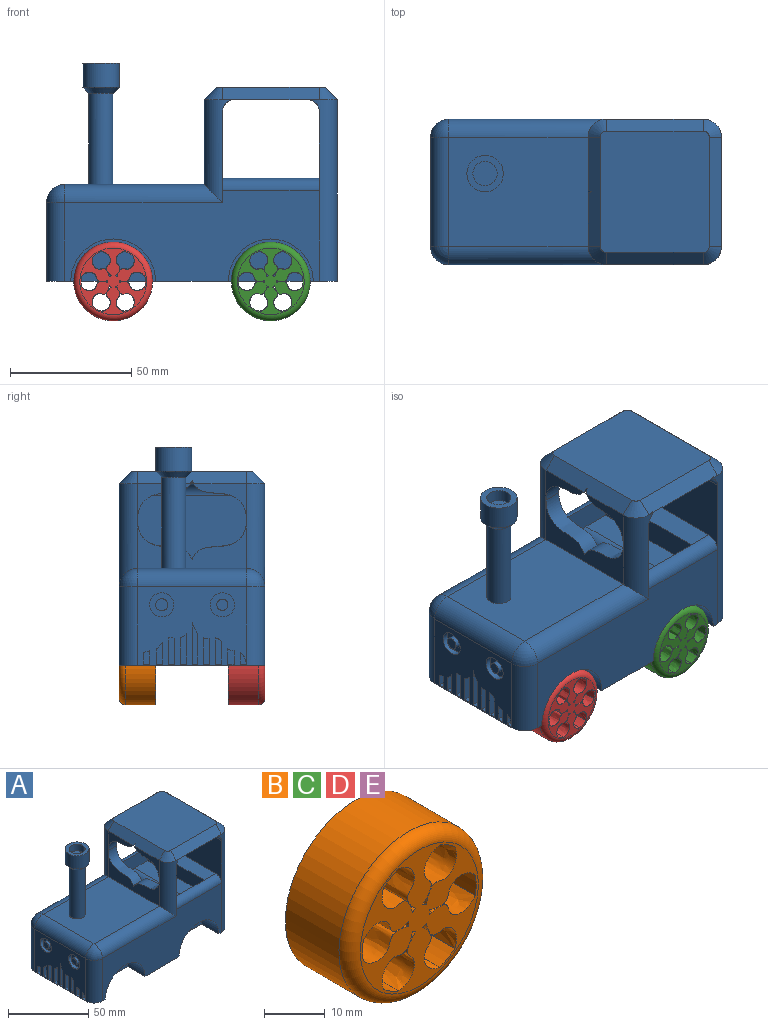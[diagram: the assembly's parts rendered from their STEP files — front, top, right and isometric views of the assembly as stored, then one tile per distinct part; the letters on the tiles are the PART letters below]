
ASSEMBLY  parts=5 mates=4
PART A: 116 faces, bbox 120.1x60.1x90.1 mm
  f0: plane 45x32.5mm, normal (-1,0,0), area 1108mm2, adj f4,f20,f22,f23,f52,f55,f56,f57
  f1: plane 22.46x15.71mm, normal (-1,0,0), area 101.4mm2, adj f18,f32,f38
  f2: plane 22.54x15.71mm, normal (-1,0,0), area 100.8mm2, adj f25,f29,f38
  f3: plane 105x37.5mm, normal (0,1,0), area 2650.4mm2, adj f4,f14,f16,f23,f25,f26,f28,f46
  f4: plane 120x60mm, normal (0,0,-1), area 5051.7mm2, adj f0,f3,f6,f7,f10,f11,f12,f13
  f5: plane 50x45mm, normal (0,0,1), area 2244.6mm2, adj f34,f35,f36,f37,f38,f39,f40,f41
  f6: plane 105x37.5mm, normal (0,-1,0), area 2650.4mm2, adj f4,f10,f12,f18,f19,f20,f27,f50
  f7: plane 75x45mm, normal (1,0,0), area 3375mm2, adj f4,f27,f28,f37
  f8: plane 57.5x45mm, normal (0,0,1), area 2509mm2, adj f9,f19,f22,f26,f103
  f9: plane 45x20mm, normal (-1,0,0), area 426.2mm2, adj f8,f18,f25,f30,f31
  f10: cylinder r=17.5mm len=35mm, axis (0,-1,0), area 824.7mm2, adj f4,f6,f11
  f11: plane 35x17.5mm, normal (0,-1,0), area 481.1mm2, adj f4,f10
  f12: cylinder r=17.5mm len=35mm, axis (0,-1,0), area 824.7mm2, adj f4,f6,f13
  f13: plane 35x17.5mm, normal (0,-1,0), area 481.1mm2, adj f4,f12
  f14: cylinder r=17.5mm len=35mm, axis (0,1,0), area 824.7mm2, adj f3,f4,f15
  f15: plane 35x17.5mm, normal (0,1,0), area 481.1mm2, adj f4,f14
  f16: cylinder r=17.5mm len=35mm, axis (0,1,0), area 824.7mm2, adj f3,f4,f17
  f17: plane 35x17.5mm, normal (0,1,0), area 481.1mm2, adj f4,f16
  f18: cylinder r=7.5mm len=42.5mm, axis (0,0,-1), area 449.9mm2, adj f1,f6,f9,f19,f40,f43,f45,f47
  f19: cylinder r=7.5mm len=65mm, axis (-1,0,0), area 709.5mm2, adj f6,f8,f18,f21
  f20: cylinder r=7.5mm len=32.5mm, axis (0,0,-1), area 382.9mm2, adj f0,f4,f6,f21
  f21: sphere r=7.5mm, area 88.4mm2, adj f19,f20,f22
  f22: cylinder r=7.5mm len=45mm, axis (0,1,0), area 530.1mm2, adj f0,f8,f21,f24
  f23: cylinder r=7.5mm len=32.5mm, axis (0,0,1), area 382.9mm2, adj f0,f3,f4,f24
  f24: sphere r=7.5mm, area 88.4mm2, adj f22,f23,f26
  f25: cylinder r=7.5mm len=42.5mm, axis (0,0,1), area 449.9mm2, adj f2,f3,f9,f26,f36,f43,f45,f49
  f26: cylinder r=7.5mm len=65mm, axis (1,0,0), area 709.5mm2, adj f3,f8,f24,f25
  f27: cylinder r=7.5mm len=75mm, axis (0,0,1), area 889.1mm2, adj f4,f6,f7,f39,f44,f45,f48
  f28: cylinder r=7.5mm len=75mm, axis (0,0,-1), area 889.1mm2, adj f3,f4,f7,f35,f44,f45,f48
  f29: extruded ~25x22.54mm, area 266.2mm2, adj f2,f30,f32,f33,f38,f43,f45,f49
  f30: extruded ~22.54x16.26mm, area 233.4mm2, adj f9,f29,f31,f43
  f31: extruded ~22.46x16.26mm, area 232.6mm2, adj f9,f30,f32,f43
  f32: extruded ~25x22.46mm, area 265.3mm2, adj f1,f29,f31,f33,f38,f43,f45,f47
  f33: plane 1.36x1.27mm, normal (-1,0,0), area 0.8mm2, adj f29,f32,f45
  f34: plane 40x5mm, normal (0,0.71,0.71), area 282.8mm2, adj f5,f35,f36,f45
  f35: cone r=2.5mm half-angle=45deg, axis (0,0,-1), area 55.5mm2, adj f5,f28,f34,f37
  f36: cone r=2.5mm half-angle=45deg, axis (0,0,-1), area 55.5mm2, adj f5,f25,f34,f38
  f37: plane 45x5mm, normal (0.71,0,0.71), area 318.2mm2, adj f5,f7,f35,f39
  f38: plane 45.05x5.05mm, normal (-0.71,0,0.71), area 317.1mm2, adj f1,f2,f5,f29,f32,f36,f40
  f39: cone r=2.5mm half-angle=45deg, axis (0,0,-1), area 55.5mm2, adj f5,f27,f37,f41
  f40: cone r=2.5mm half-angle=45deg, axis (0,0,-1), area 55.5mm2, adj f5,f18,f38,f41
  f41: plane 40x5mm, normal (0,-0.71,0.71), area 282.8mm2, adj f5,f39,f40,f45
  f42: plane 50x10.25mm, normal (0,0,1), area 512.5mm2, adj f44,f46,f50,f113
  f43: plane 60x52.85mm, normal (1,0,0), area 2018.2mm2, adj f18,f25,f29,f30,f31,f32,f46,f47
  f44: plane 60x32.5mm, normal (-1,0,0), area 1660.7mm2, adj f27,f28,f42,f46,f48,f50
  f45: plane 60x40mm, normal (0,0,-1), area 1795.2mm2, adj f18,f25,f27,f28,f29,f32,f33,f34
  f46: cylinder r=5mm len=40mm, axis (1,0,0), area 314.2mm2, adj f3,f42,f43,f44,f110
  f47: cylinder r=5mm len=29.29mm, axis (0,1,0), area 201.9mm2, adj f18,f32,f43,f45
  f48: cylinder r=5mm len=60mm, axis (0,1,0), area 464.8mm2, adj f27,f28,f44,f45
  f49: cylinder r=5mm len=29.36mm, axis (0,1,0), area 201.7mm2, adj f25,f29,f43,f45
  f50: cylinder r=5mm len=40mm, axis (-1,0,0), area 314.2mm2, adj f6,f42,f43,f44,f111
  f51: cylinder r=2.5mm len=5mm, axis (-1,0,0), area 39.3mm2, adj f53,f54
  f52: cylinder r=5mm len=10mm, axis (-1,0,0), area 78.5mm2, adj f0,f53
  f53: plane 10x10mm, normal (-1,0,0), area 58.9mm2, adj f51,f52
  f54: plane 5x5mm, normal (-1,0,0), area 19.6mm2, adj f51
  f55: extruded ~4.84x2.5mm, area 14.2mm2, adj f0,f56,f57,f58
  f56: plane 4.84x2.5mm, normal (0,-1,0), area 12.1mm2, adj f0,f55,f57,f58
  f57: plane 2.5x2.5mm, normal (0,0,1), area 6.2mm2, adj f0,f55,f56,f58
  f58: plane 4.84x2.5mm, normal (-1,0,0), area 8.6mm2, adj f55,f56,f57
  f59: plane 6.29x2.5mm, normal (0,-1,0), area 15.7mm2, adj f0,f60,f62,f63
  f60: plane 2.5x2.5mm, normal (0,0,1), area 6.2mm2, adj f0,f59,f61,f63
  f61: plane 5.49x2.5mm, normal (0,1,0), area 13.7mm2, adj f0,f60,f62,f63
  f62: extruded ~2.5x2.5mm, area 6.6mm2, adj f0,f59,f61,f63
  f63: plane 6.29x2.5mm, normal (-1,0,0), area 14.5mm2, adj f59,f60,f61,f62
  f64: plane 10.81x2.5mm, normal (0,-1,0), area 27mm2, adj f0,f65,f67,f68
  f65: plane 2.5x2.5mm, normal (0,0,1), area 6.2mm2, adj f0,f64,f66,f68
  f66: plane 10.79x2.5mm, normal (0,1,0), area 27mm2, adj f0,f65,f67,f68
  f67: extruded ~2.5x2.5mm, area 6.3mm2, adj f0,f64,f66,f68
  f68: plane 10.92x2.5mm, normal (-1,0,0), area 27.1mm2, adj f64,f65,f66,f67
  f69: plane 6.29x2.5mm, normal (0,-1,0), area 15.7mm2, adj f0,f70,f72,f73
  f70: plane 2.5x2.5mm, normal (0,0,1), area 6.2mm2, adj f0,f69,f71,f73
  f71: plane 9.01x2.5mm, normal (0,1,0), area 22.5mm2, adj f0,f70,f72,f73
  f72: extruded ~2.72x2.5mm, area 9.3mm2, adj f0,f69,f71,f73
  f73: plane 9.01x2.5mm, normal (-1,0,0), area 18.8mm2, adj f69,f70,f71,f72
  f74: plane 4.84x2.5mm, normal (0,-1,0), area 12.1mm2, adj f0,f75,f77,f78
  f75: plane 2.5x2.5mm, normal (0,0,1), area 6.2mm2, adj f0,f74,f76,f78
  f76: plane 5.49x2.5mm, normal (0,1,0), area 13.7mm2, adj f0,f75,f77,f78
  f77: extruded ~2.5x2.5mm, area 6.5mm2, adj f0,f74,f76,f78
  f78: plane 5.49x2.5mm, normal (-1,0,0), area 13.1mm2, adj f74,f75,f76,f77
  f79: cylinder r=2.29mm len=4.58mm, axis (-1,0,0), area 36mm2, adj f81,f82
  f80: cylinder r=5mm len=10mm, axis (-1,0,0), area 78.5mm2, adj f0,f81
  f81: plane 10x10mm, normal (-1,0,0), area 62.1mm2, adj f79,f80
  f82: plane 4.58x4.58mm, normal (-1,0,0), area 16.5mm2, adj f79
  f83: plane 10.85x2.5mm, normal (0,-1,0), area 27.1mm2, adj f0,f84,f86,f87
  f84: plane 2.5x2.5mm, normal (0,0,1), area 6.2mm2, adj f0,f83,f85,f87
  f85: plane 12.71x2.5mm, normal (0,1,0), area 31.8mm2, adj f0,f84,f86,f87
  f86: extruded ~2.5x2.5mm, area 7.9mm2, adj f0,f83,f85,f87
  f87: plane 12.71x2.5mm, normal (-1,0,0), area 28.9mm2, adj f83,f84,f85,f86
  f88: plane 17x2.5mm, normal (0,-1,0), area 42.5mm2, adj f0,f89,f91,f92
  f89: plane 2.5x2.33mm, normal (0,0,1), area 5.8mm2, adj f0,f88,f90,f92
  f90: plane 12.71x2.5mm, normal (0,1,0), area 31.8mm2, adj f0,f89,f91,f92
  f91: extruded ~4.29x2.5mm, area 12.2mm2, adj f0,f88,f90,f92
  f92: plane 17x2.33mm, normal (-1,0,0), area 34.1mm2, adj f88,f89,f90,f91
  f93: plane 10.85x2.5mm, normal (0,-1,0), area 27.1mm2, adj f0,f94,f96,f97
  f94: plane 2.5x2.5mm, normal (0,0,1), area 6.2mm2, adj f0,f93,f95,f97
  f95: plane 10.79x2.5mm, normal (0,1,0), area 27mm2, adj f0,f94,f96,f97
  f96: extruded ~2.5x2.5mm, area 6.3mm2, adj f0,f93,f95,f97
  f97: plane 10.85x2.5mm, normal (-1,0,0), area 26.9mm2, adj f93,f94,f95,f96
  f98: plane 10.81x2.5mm, normal (0,-1,0), area 27mm2, adj f0,f99,f101,f102
  f99: plane 2.5x2.5mm, normal (0,0,1), area 6.2mm2, adj f0,f98,f100,f102
  f100: plane 9.01x2.5mm, normal (0,1,0), area 22.5mm2, adj f0,f99,f101,f102
  f101: extruded ~2.5x2.5mm, area 7.9mm2, adj f0,f98,f100,f102
  f102: plane 10.81x2.5mm, normal (-1,0,0), area 25.4mm2, adj f98,f99,f100,f101
  f103: cylinder r=5mm len=37.5mm, axis (0,0,-1), area 1178.1mm2, adj f8,f106
  f104: cylinder r=7.5mm len=15mm, axis (0,0,-1), area 471.2mm2, adj f105,f106
  f105: plane 15x15mm, normal (0,0,1), area 98.2mm2, adj f104,f107
  f106: cone r=7.5mm half-angle=45deg, axis (0,0,1), area 138.8mm2, adj f103,f104
  f107: cylinder r=5mm len=10mm, axis (0,0,1), area 157.1mm2, adj f105,f108
  f108: plane 10x10mm, normal (0,0,1), area 78.5mm2, adj f107
  f109: plane 50x10mm, normal (-1,0,0), area 500mm2, adj f110,f111,f112,f115
  f110: plane 29.75x25mm, normal (0,-1,0), area 502.3mm2, adj f43,f46,f109,f112,f113,f114,f115
  f111: plane 29.75x25mm, normal (0,1,0), area 502.3mm2, adj f43,f50,f109,f112,f113,f114,f115
  f112: plane 50x13.3mm, normal (0,0,1), area 664.8mm2, adj f43,f109,f110,f111
  f113: plane 50x10mm, normal (-1,0,0), area 500mm2, adj f42,f110,f111,f114
  f114: plane 50x11.45mm, normal (0,0,1), area 572.7mm2, adj f110,f111,f113,f115
  f115: cylinder r=5mm len=50mm, axis (0,-1,0), area 392.7mm2, adj f109,f110,f111,f114
PART B: 28 faces, bbox 35.2x15x35.2 mm
  f0: cylinder r=13.25mm len=15mm, axis (0,1,0), area 61.5mm2, adj f16,f17,f25,f26
  f1: cylinder r=13.25mm len=15mm, axis (0,1,0), area 61.5mm2, adj f14,f15,f25,f26
  f2: cylinder r=13.25mm len=15mm, axis (0,1,0), area 61.5mm2, adj f12,f13,f25,f26
  f3: cylinder r=13.25mm len=15mm, axis (0,1,0), area 61.5mm2, adj f10,f11,f25,f26
  f4: cylinder r=13.25mm len=15mm, axis (0,1,0), area 61.5mm2, adj f8,f9,f25,f26
  f5: cylinder r=13.25mm len=15mm, axis (0,1,0), area 61.5mm2, adj f7,f18,f25,f26
  f6: cylinder r=16.25mm len=32.5mm, axis (0,1,0), area 1276.3mm2, adj f25,f27
  f7: extruded ~15x9.99mm, area 196.8mm2, adj f5,f24,f25,f26
  f8: extruded ~15x9.99mm, area 196.8mm2, adj f4,f19,f25,f26
  f9: extruded ~15x8.43mm, area 196.8mm2, adj f4,f19,f25,f26
  f10: extruded ~15x10.64mm, area 196.8mm2, adj f3,f20,f25,f26
  f11: extruded ~15x10.64mm, area 196.8mm2, adj f3,f20,f25,f26
  f12: extruded ~15x8.43mm, area 196.8mm2, adj f2,f21,f25,f26
  f13: extruded ~15x9.99mm, area 196.8mm2, adj f2,f21,f25,f26
  f14: extruded ~15x9.99mm, area 196.8mm2, adj f1,f22,f25,f26
  f15: extruded ~15x8.43mm, area 196.8mm2, adj f1,f22,f25,f26
  f16: extruded ~15x10.64mm, area 196.8mm2, adj f0,f23,f25,f26
  f17: extruded ~15x10.64mm, area 196.8mm2, adj f0,f23,f25,f26
  f18: extruded ~15x8.43mm, area 196.8mm2, adj f5,f24,f25,f26
  f19: cylinder r=2.5mm len=15mm, axis (0,1,0), area 14.5mm2, adj f8,f9,f25,f26
  f20: cylinder r=2.5mm len=15mm, axis (0,1,0), area 14.5mm2, adj f10,f11,f25,f26
  f21: cylinder r=2.5mm len=15mm, axis (0,1,0), area 14.5mm2, adj f12,f13,f25,f26
  f22: cylinder r=2.5mm len=15mm, axis (0,1,0), area 14.5mm2, adj f14,f15,f25,f26
  f23: cylinder r=2.5mm len=15mm, axis (0,1,0), area 14.5mm2, adj f16,f17,f25,f26
  f24: cylinder r=2.5mm len=15mm, axis (0,1,0), area 14.5mm2, adj f7,f18,f25,f26
  f25: plane 32.5x32.5mm, normal (0,1,0), area 570mm2, adj f0,f1,f2,f3,f4,f5,f6,f7
  f26: plane 27.5x27.5mm, normal (0,-1,0), area 334.3mm2, adj f0,f1,f2,f3,f4,f5,f7,f8
  f27: torus R=13.75mm, axis (0,-1,0), area 378.5mm2, adj f6,f26
PART C: same geometry as B
PART D: same geometry as B
PART E: same geometry as B
PLACE A t=(-99.54,-36.7,16.35)mm
PLACE B rot(axis=(0,0,1),180deg) t=(-132.04,-21.7,16.35)mm
PLACE C t=(-67.04,-51.7,16.35)mm
PLACE D t=(-132.04,-51.7,16.35)mm
PLACE E rot(axis=(0,0,1),180deg) t=(-67.04,-21.7,16.35)mm
MATE fastened E.f6 <-> A.f14  axis (0,-1,0) through (-67.04,-21.7,16.35)mm
MATE fastened B.f6 <-> A.f16  axis (0,-1,0) through (-132.04,-21.7,16.35)mm
MATE fastened A.f10 <-> C.f6  axis (0,-1,0) through (-67.04,-51.7,16.35)mm
MATE fastened A.f12 <-> D.f6  axis (0,-1,0) through (-132.04,-51.7,16.35)mm
